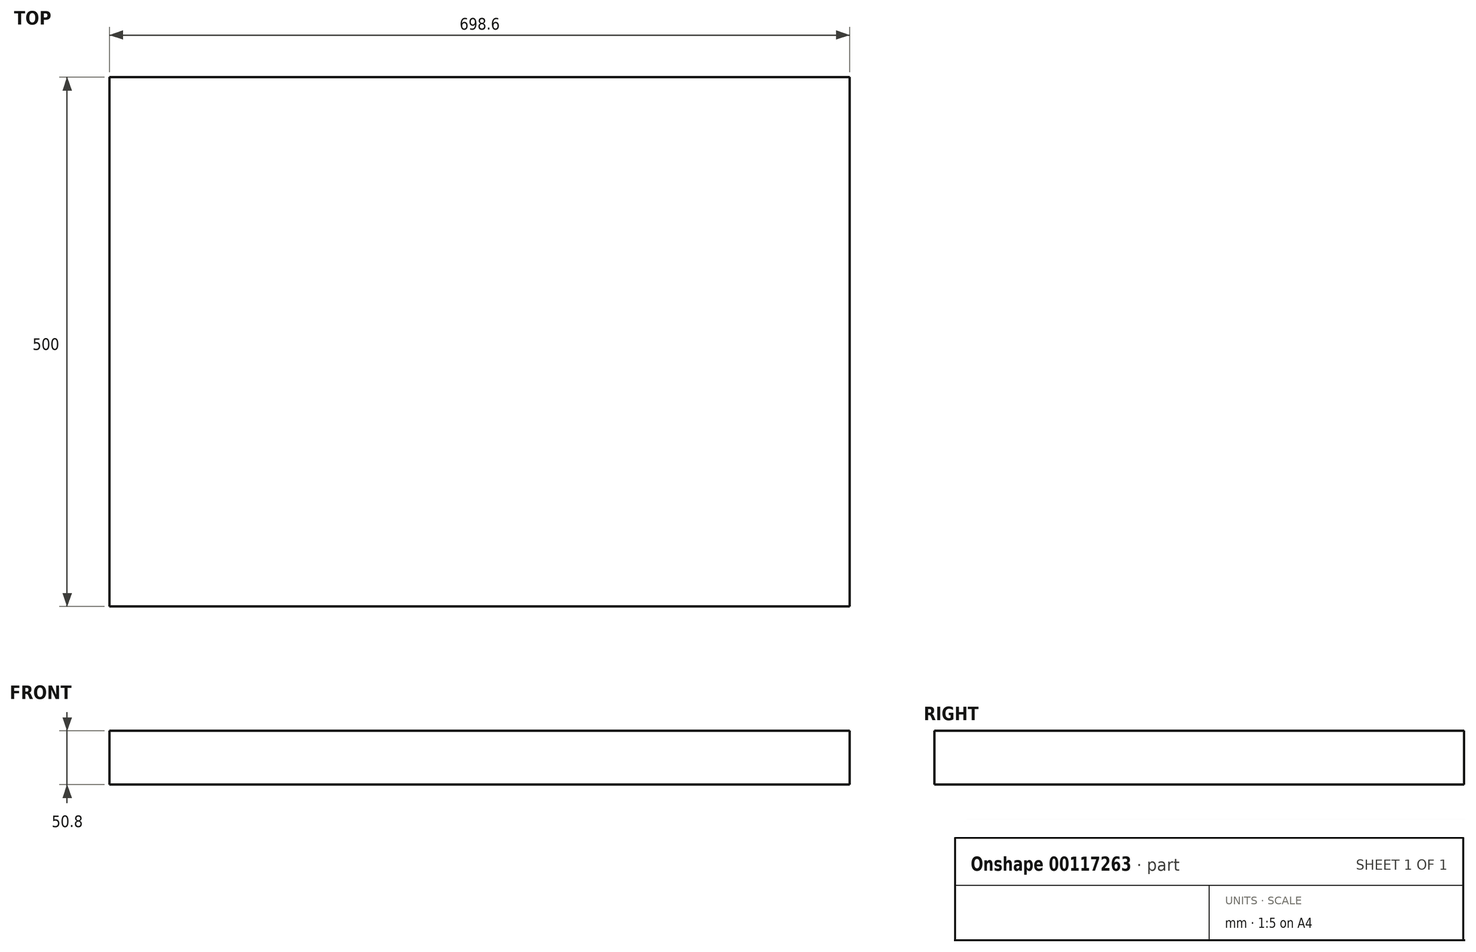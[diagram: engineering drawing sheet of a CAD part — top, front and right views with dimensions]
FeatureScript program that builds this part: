
annotation { "Feature Type Name" : "Feature", "Feature Type Description" : "" }
export const myFeature = defineFeature(function(context is Context, id is Id, definition is map)
    precondition{}
    {
        {
            var Q0;
            Q0=qCreatedBy(makeId("Top.planeOp"),FACE);
            var sketch = newSketch(context, id + "F0", { "sketchPlane" : qUnion([Q0])});
            skLineSegment(sketch, "E0.bottom", {"start": v(-332.06, 253.65) * mm, "end": v(366.54, 253.65) * mm});
            skLineSegment(sketch, "E0.top", {"start": v(-332.06, -246.35) * mm, "end": v(366.54, -246.35) * mm});
            skLineSegment(sketch, "E0.left", {"start": v(-332.06, 253.65) * mm, "end": v(-332.06, -246.35) * mm});
            skLineSegment(sketch, "E0.right", {"start": v(366.54, 253.65) * mm, "end": v(366.54, -246.35) * mm});
            skSolve(sketch);
        }
        {
            var Q0;
            Q0=makeQuery(id+"F0.imprint","IMPRINT",FACE,{"disambiguationData":[TD([[makeQuery(id+"F0.imprint","IMPRINT",EDGE,{"derivedFrom":sQuery(id+"F0.wireOp",EDGE,"E0.bottom")}),-1.0]])]});
            extrude(context, id + "F1", {"entities" : qUnion([Q0]), "depth" : 50.8 * mm, "offsetDistance" : 25 * mm});
        }
    });
